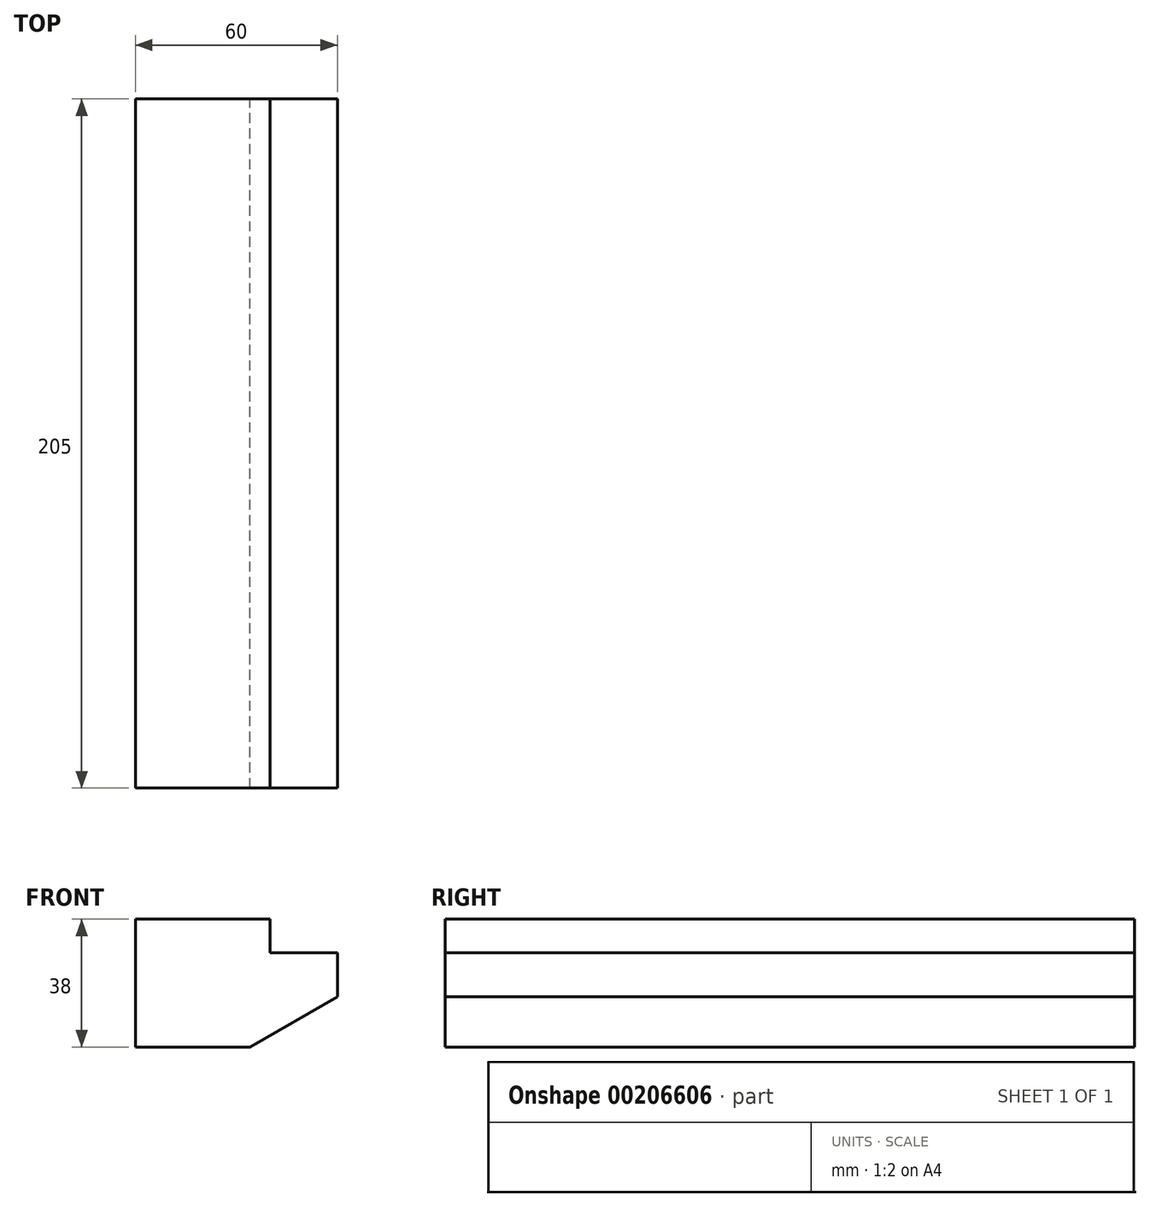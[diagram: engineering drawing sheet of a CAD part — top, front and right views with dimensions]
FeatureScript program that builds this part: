
annotation { "Feature Type Name" : "Feature", "Feature Type Description" : "" }
export const myFeature = defineFeature(function(context is Context, id is Id, definition is map)
    precondition{}
    {
        {
            var Q0;
            Q0=qCreatedBy(makeId("Front.planeOp"),FACE);
            var sketch = newSketch(context, id + "F0", { "sketchPlane" : qUnion([Q0])});
            skLineSegment(sketch, "E0.bottom", {"start": v(0, 0) * mm, "end": v(34.02, 0) * mm});
            skLineSegment(sketch, "E0.top", {"start": v(0, 38) * mm, "end": v(40, 38) * mm});
            skLineSegment(sketch, "E0.left", {"start": v(0, 0) * mm, "end": v(0, 38) * mm});
            skLineSegment(sketch, "E0.right", {"start": v(60, 15) * mm, "end": v(60, 28) * mm});
            skLineSegment(sketch, "E1", {"start": v(40, 38) * mm, "end": v(40, 28) * mm});
            skLineSegment(sketch, "E2", {"start": v(40, 28) * mm, "end": v(60, 28) * mm});
            skLineSegment(sketch, "E3", {"start": v(60, 15) * mm, "end": v(34.02, 0) * mm});
            skSolve(sketch);
        }
        {
            var Q0;
            Q0 = qSketchRegion(id + "F0", true);
            extrude(context, id + "F1", {"entities" : qUnion([Q0]), "depth" : 205 * mm});
        }
    });
